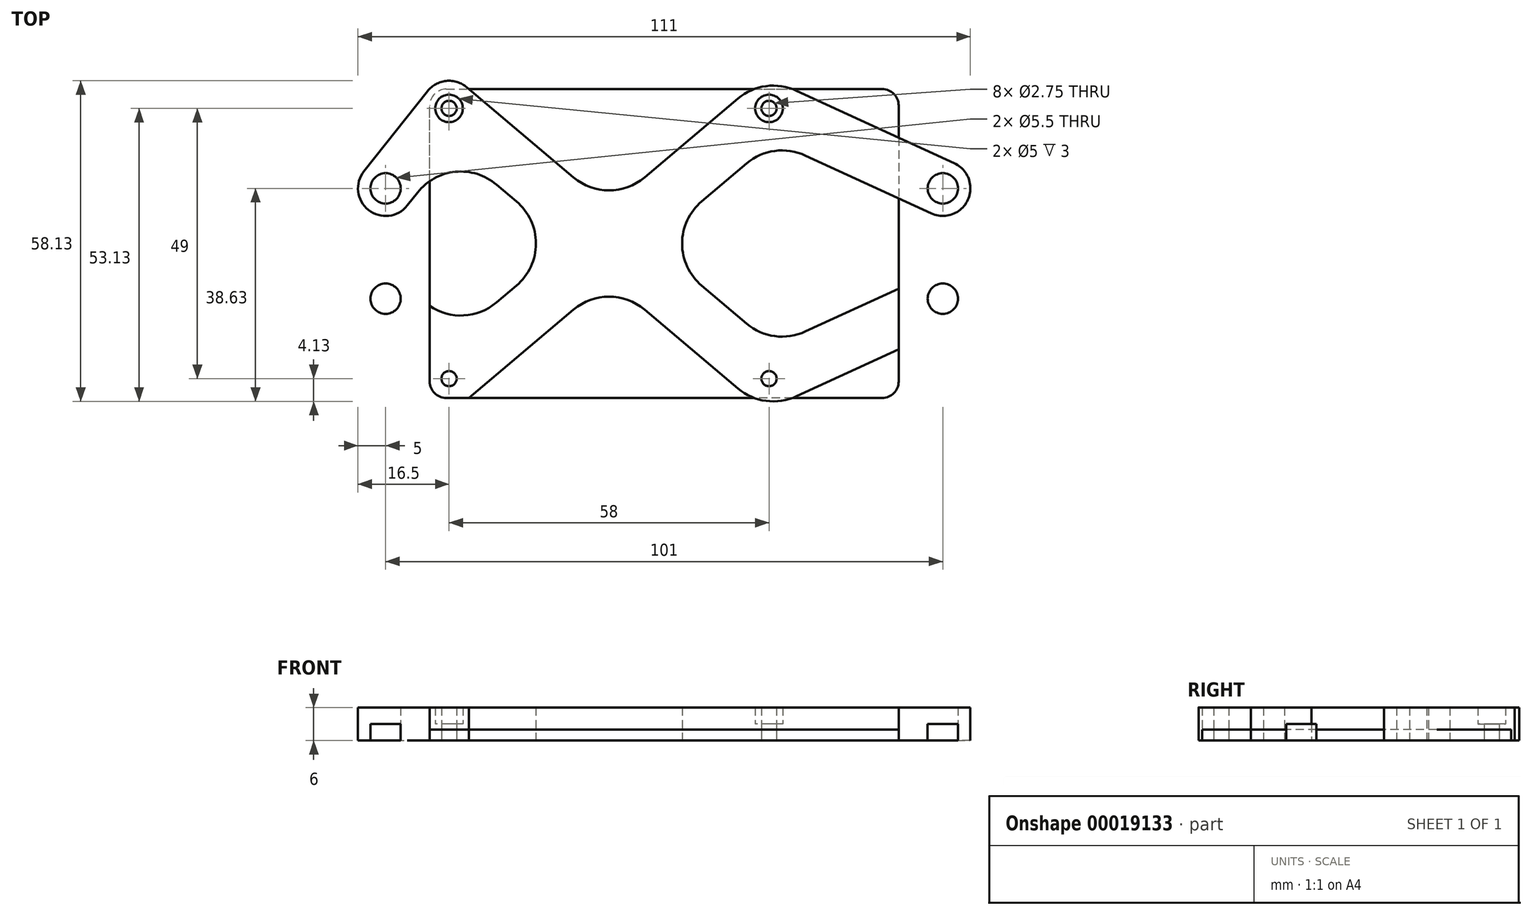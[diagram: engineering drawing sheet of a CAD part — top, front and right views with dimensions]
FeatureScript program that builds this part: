
annotation { "Feature Type Name" : "Feature", "Feature Type Description" : "" }
export const myFeature = defineFeature(function(context is Context, id is Id, definition is map)
    precondition{}
    {
        {
            var Q0;
            Q0=qCreatedBy(makeId("Top.planeOp"),FACE);
            var sketch = newSketch(context, id + "F0", { "sketchPlane" : qUnion([Q0])});
            skLineSegment(sketch, "E0.bottom", {"start": v(0, 0) * mm, "end": v(-32.5, 0) * mm, "construction": true});
            skLineSegment(sketch, "E0.top", {"start": v(0, 28) * mm, "end": v(-29.5, 28) * mm});
            skLineSegment(sketch, "E0.left", {"start": v(0, 0) * mm, "end": v(0, 28) * mm, "construction": true});
            skLineSegment(sketch, "E0.right", {"start": v(-32.5, 0) * mm, "end": v(-32.5, 25) * mm});
            skCircle(sketch, "E1", {"center": v(-29, 24.5) * mm, "radius": 1.38 * mm});
            skCircle(sketch, "E2", {"center": v(-40.5, 10) * mm, "radius": 2.75 * mm});
            skLineSegment(sketch, "E3.MirrorCS", {"start": v(0, 0) * mm, "end": v(32.5, 0) * mm, "construction": true});
            skCircle(sketch, "E4.MirrorC", {"center": v(29, 24.5) * mm, "radius": 1.38 * mm});
            skLineSegment(sketch, "E5.MirrorCS", {"start": v(32.5, 0) * mm, "end": v(32.5, 28) * mm, "construction": true});
            skLineSegment(sketch, "E6.MirrorCS", {"start": v(0, 28) * mm, "end": v(32.5, 28) * mm});
            skLineSegment(sketch, "E7.MirrorCS", {"start": v(0, -28) * mm, "end": v(32.5, -28) * mm});
            skCircle(sketch, "E8.MirrorC", {"center": v(29, -24.5) * mm, "radius": 1.38 * mm});
            skLineSegment(sketch, "E9.MirrorCS", {"start": v(0, -28) * mm, "end": v(-29.5, -28) * mm});
            skCircle(sketch, "E10.MirrorC", {"center": v(-29, -24.5) * mm, "radius": 1.38 * mm});
            skCircle(sketch, "E11.MirrorC", {"center": v(-40.5, -10) * mm, "radius": 2.75 * mm});
            skLineSegment(sketch, "E12.MirrorCS", {"start": v(32.5, 0) * mm, "end": v(32.5, -28) * mm, "construction": true});
            skLineSegment(sketch, "E13.MirrorCS", {"start": v(-32.5, 0) * mm, "end": v(-32.5, -25) * mm});
            skLineSegment(sketch, "E14.bottom", {"start": v(32.5, 28) * mm, "end": v(49.5, 28) * mm});
            skLineSegment(sketch, "E14.top", {"start": v(32.5, -28) * mm, "end": v(49.5, -28) * mm});
            skLineSegment(sketch, "E14.left", {"start": v(32.5, 28) * mm, "end": v(32.5, -28) * mm, "construction": true});
            skLineSegment(sketch, "E14.right", {"start": v(52.5, 25) * mm, "end": v(52.5, -25) * mm});
            skPoint(sketch, "E15.visualSharp", {"position": v(52.5, 28) * mm});
            skArc(sketch, "E15.filletArc", {"start": v(52.5, 25) * mm, "mid": v(51.62, 27.12) * mm, "end": v(49.5, 28) * mm});
            skPoint(sketch, "E16.visualSharp", {"position": v(52.5, -28) * mm});
            skArc(sketch, "E16.filletArc", {"start": v(49.5, -28) * mm, "mid": v(51.62, -27.12) * mm, "end": v(52.5, -25) * mm});
            skPoint(sketch, "E17.visualSharp", {"position": v(-32.5, -28) * mm});
            skArc(sketch, "E17.filletArc", {"start": v(-32.5, -25) * mm, "mid": v(-31.62, -27.12) * mm, "end": v(-29.5, -28) * mm});
            skPoint(sketch, "E18.visualSharp", {"position": v(-32.5, 28) * mm});
            skArc(sketch, "E18.filletArc", {"start": v(-29.5, 28) * mm, "mid": v(-31.62, 27.12) * mm, "end": v(-32.5, 25) * mm});
            skCircle(sketch, "E19", {"center": v(60.5, 10) * mm, "radius": 2.75 * mm});
            skCircle(sketch, "E20.MirrorC", {"center": v(60.5, -10) * mm, "radius": 2.75 * mm});
            skLineSegment(sketch, "E21", {"start": v(0, 0) * mm, "end": v(29, 24.5) * mm, "construction": true});
            skLineSegment(sketch, "E22", {"start": v(60.5, 10) * mm, "end": v(29, 24.5) * mm, "construction": true});
            skLineSegment(sketch, "E23.0", {"start": v(16.79, 7.64) * mm, "end": v(24.94, 14.52) * mm});
            skLineSegment(sketch, "E24.0", {"start": v(58.4, 5.46) * mm, "end": v(35.57, 15.97) * mm});
            skLineSegment(sketch, "E25.0", {"start": v(6.45, 12) * mm, "end": v(23.34, 26.27) * mm});
            skLineSegment(sketch, "E26.0", {"start": v(62.6, 14.54) * mm, "end": v(33.98, 27.71) * mm});
            skArc(sketch, "E27", {"start": v(62.6, 14.54) * mm, "mid": v(65.04, 7.9) * mm, "end": v(58.4, 5.46) * mm});
            skLineSegment(sketch, "E28", {"start": v(0, 0) * mm, "end": v(-29, 24.5) * mm, "construction": true});
            skLineSegment(sketch, "E29", {"start": v(-29, 24.5) * mm, "end": v(-25.03, 29.5) * mm, "construction": true});
            skLineSegment(sketch, "E30.0", {"start": v(-36.58, 6.9) * mm, "end": v(-34.7, 9.27) * mm});
            skLineSegment(sketch, "E31.0", {"start": v(-44.42, 13.1) * mm, "end": v(-32.92, 27.6) * mm});
            skLineSegment(sketch, "E32.0", {"start": v(-6.45, 12) * mm, "end": v(-25.77, 28.32) * mm});
            skLineSegment(sketch, "E33.0", {"start": v(-16.79, 7.64) * mm, "end": v(-20.4, 10.7) * mm});
            skArc(sketch, "E34", {"start": v(-36.58, 6.9) * mm, "mid": v(-43.6, 6.08) * mm, "end": v(-44.42, 13.1) * mm});
            skLineSegment(sketch, "E35.MirrorCS", {"start": v(-16.79, -7.64) * mm, "end": v(-20.4, -10.7) * mm});
            skLineSegment(sketch, "E36.MirrorCS", {"start": v(-6.45, -12) * mm, "end": v(-25.77, -28.32) * mm});
            skLineSegment(sketch, "E37.MirrorCS", {"start": v(6.45, -12) * mm, "end": v(23.34, -26.27) * mm});
            skLineSegment(sketch, "E38.MirrorCS", {"start": v(16.79, -7.64) * mm, "end": v(24.94, -14.52) * mm});
            skLineSegment(sketch, "E39.MirrorCS", {"start": v(62.6, -14.54) * mm, "end": v(33.98, -27.71) * mm});
            skLineSegment(sketch, "E40.MirrorCS", {"start": v(58.4, -5.46) * mm, "end": v(35.57, -15.97) * mm});
            skArc(sketch, "E41.MirrorCS", {"start": v(62.6, -14.54) * mm, "mid": v(65.04, -7.9) * mm, "end": v(58.4, -5.46) * mm});
            skArc(sketch, "E42.MirrorCS", {"start": v(-36.58, -6.9) * mm, "mid": v(-43.6, -6.08) * mm, "end": v(-44.42, -13.1) * mm});
            skLineSegment(sketch, "E43.MirrorCS", {"start": v(-36.58, -6.9) * mm, "end": v(-34.7, -9.27) * mm});
            skLineSegment(sketch, "E44.MirrorCS", {"start": v(-44.42, -13.1) * mm, "end": v(-32.92, -27.6) * mm});
            skPoint(sketch, "E45.visualSharp", {"position": v(-7.75, 0) * mm});
            skArc(sketch, "E45.filletArc", {"start": v(-16.79, -7.64) * mm, "mid": v(-13.24, 0) * mm, "end": v(-16.79, 7.64) * mm});
            skPoint(sketch, "E46.visualSharp", {"position": v(0, 6.55) * mm});
            skArc(sketch, "E46.filletArc", {"start": v(-6.45, 12) * mm, "mid": v(0, 9.64) * mm, "end": v(6.45, 12) * mm});
            skPoint(sketch, "E47.visualSharp", {"position": v(7.75, 0) * mm});
            skArc(sketch, "E47.filletArc", {"start": v(16.79, 7.64) * mm, "mid": v(13.24, 0) * mm, "end": v(16.79, -7.64) * mm});
            skPoint(sketch, "E48.visualSharp", {"position": v(0, -6.55) * mm});
            skArc(sketch, "E48.filletArc", {"start": v(6.45, -12) * mm, "mid": v(0, -9.64) * mm, "end": v(-6.45, -12) * mm});
            skPoint(sketch, "E49.visualSharp", {"position": v(-29.71, -31.65) * mm});
            skPoint(sketch, "E50.visualSharp", {"position": v(28.2, -30.37) * mm});
            skArc(sketch, "E50.filletArc", {"start": v(23.34, -26.27) * mm, "mid": v(28.45, -28.54) * mm, "end": v(33.98, -27.71) * mm});
            skArc(sketch, "E51.filletArc", {"start": v(24.94, -14.52) * mm, "mid": v(30.05, -16.8) * mm, "end": v(35.57, -15.97) * mm});
            skPoint(sketch, "E52.visualSharp", {"position": v(29.8, 18.63) * mm});
            skArc(sketch, "E52.filletArc", {"start": v(35.57, 15.97) * mm, "mid": v(30.05, 16.8) * mm, "end": v(24.94, 14.52) * mm});
            skPoint(sketch, "E53.visualSharp", {"position": v(28.2, 30.37) * mm});
            skArc(sketch, "E53.filletArc", {"start": v(33.98, 27.71) * mm, "mid": v(28.45, 28.54) * mm, "end": v(23.34, 26.27) * mm});
            skPoint(sketch, "E54.visualSharp", {"position": v(-28.29, -17.35) * mm});
            skPoint(sketch, "E55.visualSharp", {"position": v(-29.71, 31.65) * mm});
            skArc(sketch, "E55.filletArc", {"start": v(-25.77, 28.32) * mm, "mid": v(-29.5, 29.48) * mm, "end": v(-32.92, 27.6) * mm});
            skPoint(sketch, "E56.visualSharp", {"position": v(-28.29, 17.35) * mm});
            skArc(sketch, "E56.filletArc", {"start": v(-20.4, 10.7) * mm, "mid": v(-27.85, 13) * mm, "end": v(-34.7, 9.27) * mm});
            skArc(sketch, "E57.filletArc", {"start": v(-32.92, -27.6) * mm, "mid": v(-29.5, -29.48) * mm, "end": v(-25.77, -28.32) * mm});
            skArc(sketch, "E58.filletArc", {"start": v(-34.7, -9.27) * mm, "mid": v(-27.85, -13) * mm, "end": v(-20.4, -10.7) * mm});
            skSolve(sketch);
        }
        {
            var Q0;
            Q0=makeQuery(id+"F0.imprint","IMPRINT",FACE,{"disambiguationData":[TD([[makeQuery(id+"F0.imprint","IMPRINT",EDGE,{"derivedFrom":sQuery(id+"F0.wireOp",EDGE,"E1")}),-1.0]])]});
            var Q1;
            Q1=makeQuery(id+"F0.imprint","IMPRINT",FACE,{"disambiguationData":[TD([[makeQuery(id+"F0.imprint","IMPRINT",EDGE,{"derivedFrom":sQuery(id+"F0.wireOp",EDGE,"E2")}),-1.0]])]});
            var Q2;
            Q2=makeQuery(id+"F0.imprint","IMPRINT",FACE,{"disambiguationData":[TD([[makeQuery(id+"F0.imprint","IMPRINT",EDGE,{"derivedFrom":sQuery(id+"F0.wireOp",EDGE,"E19")}),-1.0]])]});
            var Q3;
            Q3=makeQuery(id+"F0.imprint","IMPRINT",FACE,{"disambiguationData":[TD([[makeQuery(id+"F0.imprint","IMPRINT",EDGE,{"derivedFrom":sQuery(id+"F0.wireOp",EDGE,"E20.MirrorC")}),1.0]])]});
            var Q4;
            Q4=makeQuery(id+"F0.imprint","IMPRINT",FACE,{"disambiguationData":[TD([[makeQuery(id+"F0.imprint","IMPRINT",EDGE,{"derivedFrom":sQuery(id+"F0.wireOp",EDGE,"E11.MirrorC")}),1.0]])]});
            var Q5;
            {var subQ1=sQuery(id+"F0.wireOp",EDGE,"E14.top");var subQ3=sQuery(id+"F0.wireOp",EDGE,"E7.MirrorCS");var subQ5=makeQuery(id+"F0.imprint","INTERSECT",VERTEX,{"derivedFrom":[subQ3,subQ1]});Q5=makeQuery(id+"F0.imprint","IMPRINT",FACE,{"disambiguationData":[TD([[makeQuery(id+"F0.imprint","IMPRINT",EDGE,{"disambiguationData":[TD([[subQ5,1.0]])],"derivedFrom":subQ3}),-1.0]])]});}
            var Q6;
            {var subQ1=sQuery(id+"F0.wireOp",EDGE,"E14.bottom");var subQ3=sQuery(id+"F0.wireOp",EDGE,"E6.MirrorCS");var subQ5=makeQuery(id+"F0.imprint","INTERSECT",VERTEX,{"derivedFrom":[subQ3,subQ1]});Q6=makeQuery(id+"F0.imprint","IMPRINT",FACE,{"disambiguationData":[TD([[makeQuery(id+"F0.imprint","IMPRINT",EDGE,{"disambiguationData":[TD([[subQ5,1.0]])],"derivedFrom":subQ3}),1.0]])]});}
            extrude(context, id + "F1", {"entities" : qUnion([Q0, Q1, Q2, Q3, Q4, Q5, Q6]), "depth" : 3 * mm});
        }
        {
            var Q0;
            Q0=makeQuery(id+"F1.opExtrude","CAP_FACE",FACE,{"disambiguationData":[OSD([sQuery(id+"F0.wireOp",EDGE,"E1"),sQuery(id+"F0.wireOp",EDGE,"E2"),sQuery(id+"F0.wireOp",EDGE,"E4.MirrorC"),sQuery(id+"F0.wireOp",EDGE,"E8.MirrorC"),sQuery(id+"F0.wireOp",EDGE,"E10.MirrorC"),sQuery(id+"F0.wireOp",EDGE,"E11.MirrorC"),sQuery(id+"F0.wireOp",EDGE,"E19"),sQuery(id+"F0.wireOp",EDGE,"E20.MirrorC"),sQuery(id+"F0.wireOp",EDGE,"E23.0"),sQuery(id+"F0.wireOp",EDGE,"E24.0"),sQuery(id+"F0.wireOp",EDGE,"E25.0"),sQuery(id+"F0.wireOp",EDGE,"E26.0"),sQuery(id+"F0.wireOp",EDGE,"E27"),sQuery(id+"F0.wireOp",EDGE,"E30.0"),sQuery(id+"F0.wireOp",EDGE,"E31.0"),sQuery(id+"F0.wireOp",EDGE,"E32.0"),sQuery(id+"F0.wireOp",EDGE,"E33.0"),sQuery(id+"F0.wireOp",EDGE,"E34"),sQuery(id+"F0.wireOp",EDGE,"E35.MirrorCS"),sQuery(id+"F0.wireOp",EDGE,"E36.MirrorCS"),sQuery(id+"F0.wireOp",EDGE,"E37.MirrorCS"),sQuery(id+"F0.wireOp",EDGE,"E38.MirrorCS"),sQuery(id+"F0.wireOp",EDGE,"E39.MirrorCS"),sQuery(id+"F0.wireOp",EDGE,"E40.MirrorCS"),sQuery(id+"F0.wireOp",EDGE,"E41.MirrorCS"),sQuery(id+"F0.wireOp",EDGE,"E42.MirrorCS"),sQuery(id+"F0.wireOp",EDGE,"E43.MirrorCS"),sQuery(id+"F0.wireOp",EDGE,"E44.MirrorCS"),sQuery(id+"F0.wireOp",EDGE,"E45.filletArc"),sQuery(id+"F0.wireOp",EDGE,"E46.filletArc"),sQuery(id+"F0.wireOp",EDGE,"E47.filletArc"),sQuery(id+"F0.wireOp",EDGE,"E48.filletArc"),sQuery(id+"F0.wireOp",EDGE,"E50.filletArc"),sQuery(id+"F0.wireOp",EDGE,"E51.filletArc"),sQuery(id+"F0.wireOp",EDGE,"E52.filletArc"),sQuery(id+"F0.wireOp",EDGE,"E53.filletArc"),sQuery(id+"F0.wireOp",EDGE,"E55.filletArc"),sQuery(id+"F0.wireOp",EDGE,"E56.filletArc"),sQuery(id+"F0.wireOp",EDGE,"E57.filletArc"),sQuery(id+"F0.wireOp",EDGE,"E58.filletArc")])],"isStart":false});
            var sketch = newSketch(context, id + "F2", { "sketchPlane" : qUnion([Q0])});
            skCircle(sketch, "E59", {"center": v(-29, -24.5) * mm, "radius": 2.5 * mm});
            skCircle(sketch, "E60", {"center": v(29, -24.5) * mm, "radius": 2.5 * mm});
            skCircle(sketch, "E61.MirrorC", {"center": v(-29, 24.5) * mm, "radius": 2.5 * mm});
            skCircle(sketch, "E62.MirrorC", {"center": v(29, 24.5) * mm, "radius": 2.5 * mm});
            skSolve(sketch);
        }
        {
            var Q0;
            Q0=makeQuery(id+"F2.imprint","IMPRINT",FACE,{"disambiguationData":[TD([[makeQuery(id+"F2.imprint","IMPRINT",EDGE,{"derivedFrom":sQuery(id+"F2.wireOp",EDGE,"E59")}),1.0]])]});
            var Q1;
            Q1=makeQuery(id+"F2.imprint","IMPRINT",FACE,{"disambiguationData":[TD([[makeQuery(id+"F2.imprint","IMPRINT",EDGE,{"derivedFrom":sQuery(id+"F2.wireOp",EDGE,"E61.MirrorC")}),-1.0]])]});
            var Q2;
            Q2=makeQuery(id+"F2.imprint","IMPRINT",FACE,{"disambiguationData":[TD([[makeQuery(id+"F2.imprint","IMPRINT",EDGE,{"derivedFrom":sQuery(id+"F2.wireOp",EDGE,"E62.MirrorC")}),-1.0]])]});
            var Q3;
            Q3=makeQuery(id+"F2.imprint","IMPRINT",FACE,{"disambiguationData":[TD([[makeQuery(id+"F2.imprint","IMPRINT",EDGE,{"derivedFrom":sQuery(id+"F2.wireOp",EDGE,"E60")}),1.0]])]});
            extrude(context, id + "F3", {"entities" : qUnion([Q0, Q1, Q2, Q3]), "operationType" : NewBodyOperationType.ADD, "depth" : 3 * mm});
        }
        {
            var Q0;
            Q0=makeQuery(id+"F0.imprint","IMPRINT",FACE,{"disambiguationData":[TD([[makeQuery(id+"F0.imprint","IMPRINT",EDGE,{"derivedFrom":sQuery(id+"F0.wireOp",EDGE,"E1")}),-1.0]])]});
            var Q1;
            {var subQ3=sQuery(id+"F0.wireOp",EDGE,"E37.MirrorCS");Q1=makeQuery(id+"F0.imprint","IMPRINT",FACE,{"disambiguationData":[TD([[makeQuery(id+"F0.imprint","IMPRINT",EDGE,{"derivedFrom":subQ3}),-1.0]])]});}
            var Q2;
            Q2=makeQuery(id+"F0.imprint","IMPRINT",FACE,{"disambiguationData":[TD([[makeQuery(id+"F0.imprint","IMPRINT",EDGE,{"derivedFrom":sQuery(id+"F0.wireOp",EDGE,"E23.0")}),-1.0]])]});
            var Q3;
            {var subQ7=sQuery(id+"F0.wireOp",EDGE,"E15.filletArc");Q3=makeQuery(id+"F0.imprint","IMPRINT",FACE,{"disambiguationData":[TD([[makeQuery(id+"F0.imprint","IMPRINT",EDGE,{"derivedFrom":subQ7}),1.0]])]});}
            var Q4;
            {var subQ7=sQuery(id+"F0.wireOp",EDGE,"E25.0");Q4=makeQuery(id+"F0.imprint","IMPRINT",FACE,{"disambiguationData":[TD([[makeQuery(id+"F0.imprint","IMPRINT",EDGE,{"derivedFrom":subQ7}),1.0]])]});}
            var Q5;
            {var subQ7=sQuery(id+"F0.wireOp",EDGE,"E33.0");Q5=makeQuery(id+"F0.imprint","IMPRINT",FACE,{"disambiguationData":[TD([[makeQuery(id+"F0.imprint","IMPRINT",EDGE,{"derivedFrom":subQ7}),1.0]])]});}
            var Q6;
            {var subQ7=sQuery(id+"F0.wireOp",EDGE,"E16.filletArc");Q6=makeQuery(id+"F0.imprint","IMPRINT",FACE,{"disambiguationData":[TD([[makeQuery(id+"F0.imprint","IMPRINT",EDGE,{"derivedFrom":subQ7}),1.0]])]});}
            extrude(context, id + "F4", {"entities" : qUnion([Q0, Q1, Q2, Q3, Q4, Q5, Q6]), "depth" : 2 * mm});
        }
    });
